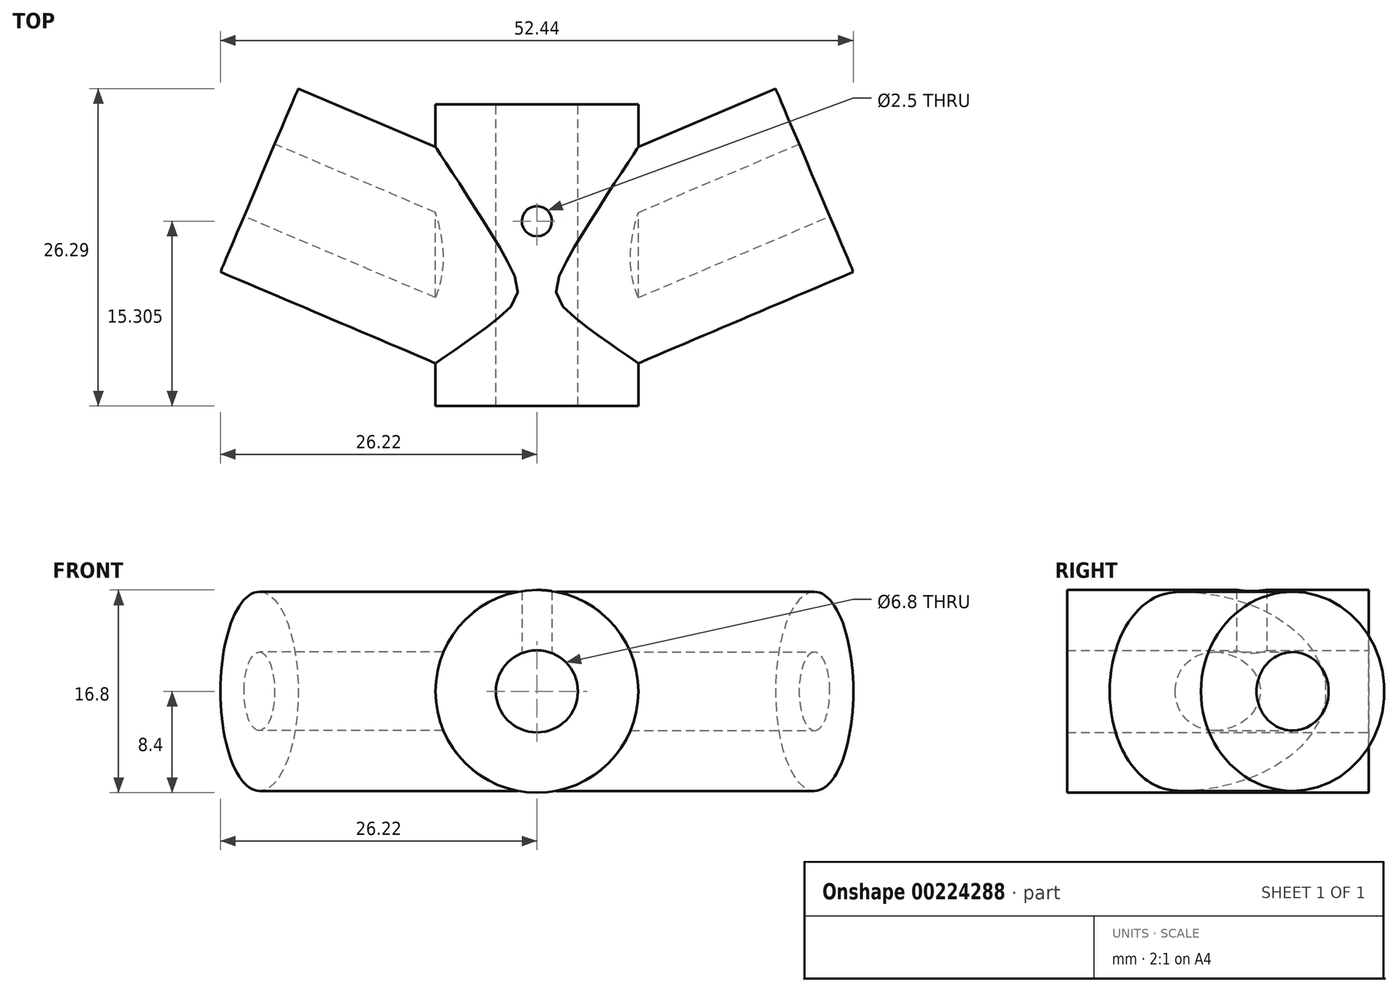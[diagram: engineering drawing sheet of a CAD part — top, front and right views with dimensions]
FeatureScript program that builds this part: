
annotation { "Feature Type Name" : "Feature", "Feature Type Description" : "" }
export const myFeature = defineFeature(function(context is Context, id is Id, definition is map)
    precondition{}
    {
        {
            var Q0;
            Q0=qCreatedBy(makeId("Front.planeOp"),FACE);
            var sketch = newSketch(context, id + "F0", { "sketchPlane" : qUnion([Q0])});
            skCircle(sketch, "E0", {"center": v(0, 0) * mm, "radius": 3.4 * mm});
            skCircle(sketch, "E1", {"center": v(0, 0) * mm, "radius": 8.4 * mm});
            skPoint(sketch, "E2", {"position": v(3.4, 0) * mm});
            skPoint(sketch, "E3", {"position": v(8.4, 0) * mm});
            skSolve(sketch);
        }
        {
            var Q0;
            Q0=makeQuery(id+"F0.imprint","IMPRINT",FACE,{"disambiguationData":[TD([[makeQuery(id+"F0.imprint","IMPRINT",EDGE,{"derivedFrom":sQuery(id+"F0.wireOp",EDGE,"E0")}),-1.0]])]});
            extrude(context, id + "F1", {"entities" : qUnion([Q0]), "endBound" : BoundingType.SYMMETRIC, "depth" : 25 * mm});
        }
        {
            var Q0;
            Q0=qCreatedBy(makeId("Top.planeOp"),FACE);
            var sketch = newSketch(context, id + "F2", { "sketchPlane" : qUnion([Q0])});
            skLineSegment(sketch, "E4", {"start": v(0, -3.57) * mm, "end": v(-23, 6.2) * mm, "construction": true});
            skPoint(sketch, "E5", {"position": v(-8.4, 0) * mm});
            skLineSegment(sketch, "E6.0", {"start": v(8.4, 12.5) * mm, "end": v(-8.4, 12.5) * mm, "construction": true});
            skLineSegment(sketch, "E7", {"start": v(-23, 6.2) * mm, "end": v(-25.14, 1.16) * mm, "construction": true});
            skSolve(sketch);
        }
        {
            var Q0;
            Q0=qCreatedBy(makeId("Right.planeOp"),FACE);
            var Q1;
            Q1=sQuery(id+"F2.wireOp",EDGE,"E7");
            cPlane(context, id + "F3", {"entities" : qUnion([Q0, Q1]), "cplaneType" : CPlaneType.LINE_ANGLE, "offset" : 25 * mm, "angle" : 0 * degree, "width" : 150 * mm, "height" : 150 * mm});
        }
        {
            var Q0;
            Q0=qCreatedBy(id+"F3.planeOp",FACE);
            var sketch = newSketch(context, id + "F4", { "sketchPlane" : qUnion([Q0])});
            skCircle(sketch, "E8", {"center": v(3.28, 0) * mm, "radius": 3.25 * mm});
            skCircle(sketch, "E9", {"center": v(3.28, 0) * mm, "radius": 8.25 * mm});
            skSolve(sketch);
        }
        {
            var Q0;
            Q0=makeQuery(id+"F4.imprint","IMPRINT",FACE,{"disambiguationData":[TD([[makeQuery(id+"F4.imprint","IMPRINT",EDGE,{"derivedFrom":sQuery(id+"F4.wireOp",EDGE,"E8")}),-1.0]])]});
            extrude(context, id + "F5", {"entities" : qUnion([Q0]), "endBound" : BoundingType.UP_TO_NEXT, "oppositeDirection" : true, "depth" : 25 * mm});
        }
        {
            var Q0;
            Q0=makeQuery(id+"F5.opExtrude","SWEPT_BODY",BODY,{"disambiguationData":[OSD([sQuery(id+"F4.wireOp",EDGE,"E8"),sQuery(id+"F4.wireOp",EDGE,"E9")])]});
            var Q1;
            Q1=qCreatedBy(makeId("Right.planeOp"),FACE);
            mirror(context, id + "F6", {"operationType" : NewBodyOperationType.ADD, "entities" : qUnion([Q0]), "mirrorPlane" : qUnion([Q1])});
        }
        {
            var Q0;
            Q0=qCreatedBy(makeId("Top.planeOp"),FACE);
            var sketch = newSketch(context, id + "F7", { "sketchPlane" : qUnion([Q0])});
            skPoint(sketch, "E10", {"position": v(0, 0) * mm});
            skPoint(sketch, "E11", {"position": v(0, 2.8) * mm});
            skSolve(sketch);
        }
        {
            var Q0;
            Q0=sQuery(id+"F7.wireOp",VERTEX,"E11");
            var Q1;
            Q1=makeQuery(id+"F1.opExtrude","SWEPT_BODY",BODY,{"disambiguationData":[OSD([sQuery(id+"F0.wireOp",EDGE,"E0"),sQuery(id+"F0.wireOp",EDGE,"E1")])]});
            hole(context, id + "F8", {"style" : HoleStyle.SIMPLE, "endStyle" : HoleEndStyle.BLIND, "oppositeDirection" : true, "holeDiameter" : 2.5 * mm, "holeDepth" : 101 * mm, "locations" : qUnion([Q0]), "scope" : qUnion([Q1])});
        }
    });
